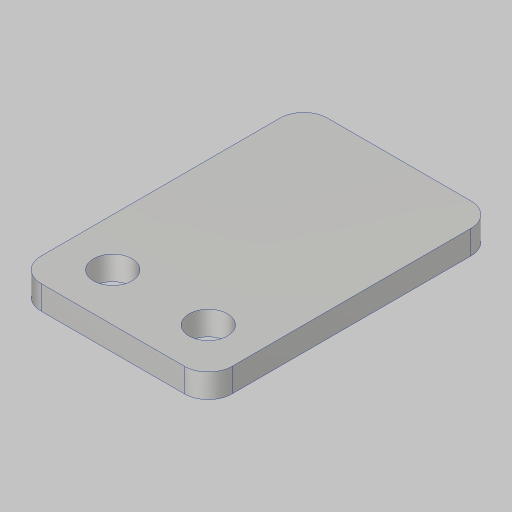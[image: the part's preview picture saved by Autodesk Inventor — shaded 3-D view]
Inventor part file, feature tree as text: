
AUTODESK INVENTOR PART (.ipt)
format: ipt  version: 2023.5 (Build 275446000, 446)  size: 137,216 bytes
history: native  units: in
note: dims shown in document units (in); Inventor stores cm internally (conversion verified against a paired STEP export)
features: sketch x1, extrude x1, hole x1, fillet x1
ambient origin geometry x8: Origin, YZ Plane, XZ Plane, XY Plane, X Axis, Y Axis, Z Axis, Center Point
bodies: Solid1 (feature_tree)
feature tree (4):
  sketch  "Sketch1"  dims[d1=0.7in d3=0.125in d4=0.197in d5=0.197in d8=1.0in d9=1.5in d10=0.25in d11=0.5in d12=0.25in d13=0.125in d14=0.0in d15=0.201in d16=0.75in d17=0.385in d18=0.25in d19=0.5635in d20=1.0in d21=0.8108in d22=0.125in d23=0.7874in d25=0.197in d26=0.3937in d28=1.0in]
  extrude  "Extrusion1"  Depth=0.125in
  hole  "Hole1"  [1 undecoded]
  fillet  "Fillet1"  Radius=0.197in
note: 1 required parameter value undecoded (feature->parameter linkage not recoverable at this tier; creation-order binding heuristic only, values carry confidence <= 0.55)
